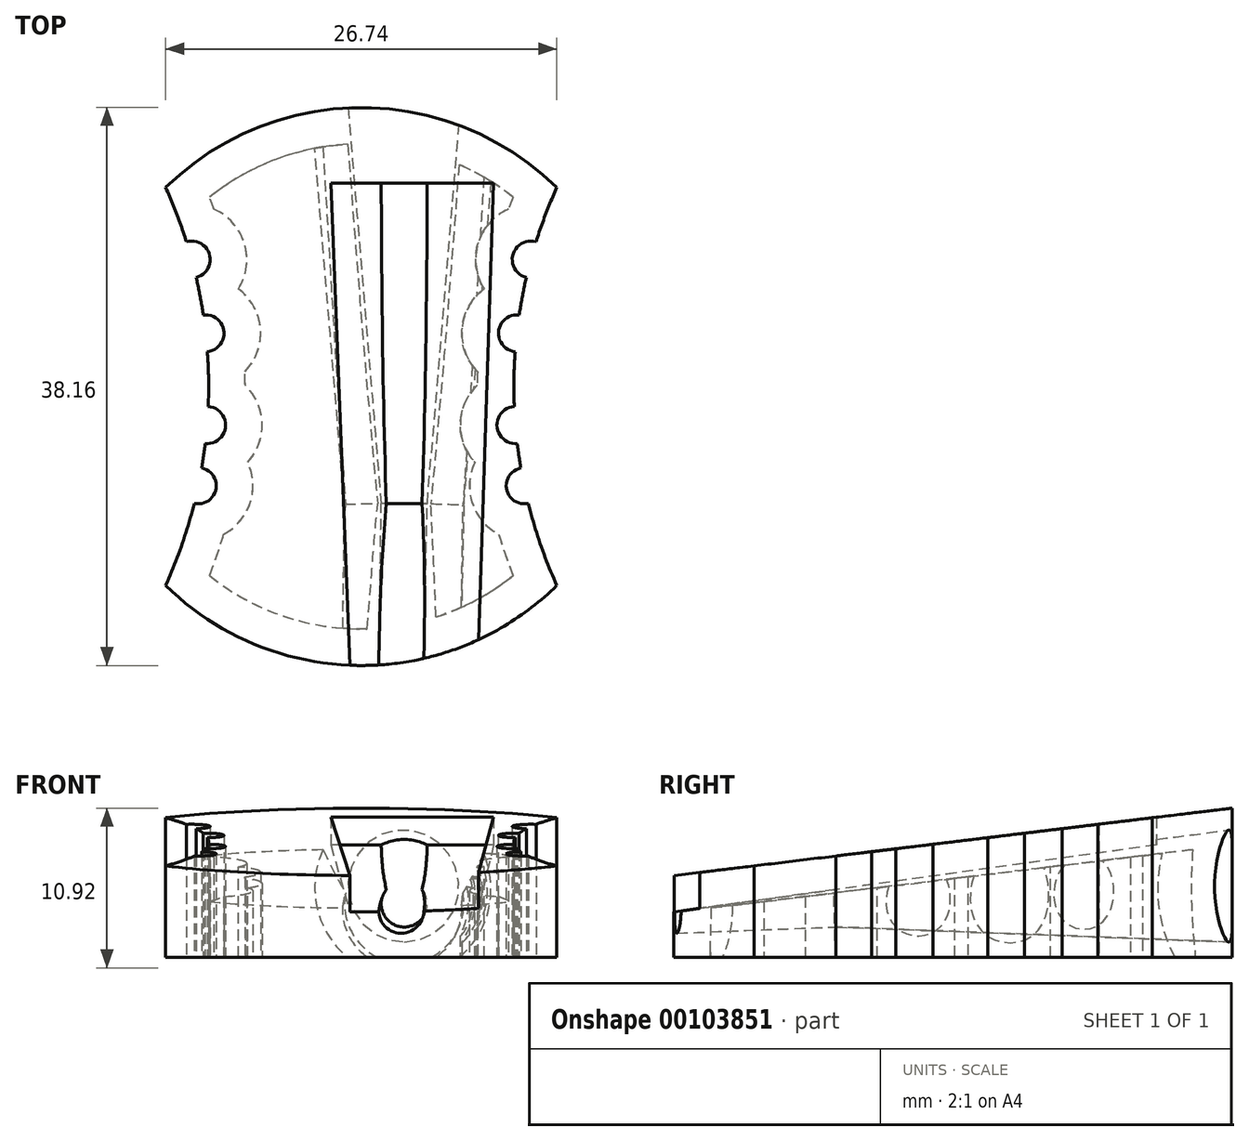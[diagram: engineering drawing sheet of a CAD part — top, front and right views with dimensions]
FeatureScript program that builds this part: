
annotation { "Feature Type Name" : "Feature", "Feature Type Description" : "" }
export const myFeature = defineFeature(function(context is Context, id is Id, definition is map)
    precondition{}
    {
        {
            var Q0;
            Q0=qCreatedBy(makeId("Top.planeOp"),FACE);
            var sketch = newSketch(context, id + "F0", { "sketchPlane" : qUnion([Q0])});
            skArc(sketch, "E0", {"start": v(-13.37, -13.61) * mm, "mid": v(-12.27, -10.85) * mm, "end": v(-11.42, -8) * mm});
            skArc(sketch, "E1", {"start": v(-13.37, -13.61) * mm, "mid": v(-7.22, -17.66) * mm, "end": v(0, -19.08) * mm});
            skLineSegment(sketch, "E2", {"start": v(0, 19.08) * mm, "end": v(0, -19.08) * mm});
            skArc(sketch, "E3.trimOffspring", {"start": v(0, 19.08) * mm, "mid": v(-7.22, 17.66) * mm, "end": v(-13.37, 13.61) * mm});
            skArc(sketch, "E4", {"start": v(-11.28, 7.44) * mm, "mid": v(-10.36, 9) * mm, "end": v(-11.95, 9.9) * mm});
            skArc(sketch, "E5", {"start": v(-10.52, 2.38) * mm, "mid": v(-9.38, 3.78) * mm, "end": v(-10.8, 4.89) * mm});
            skArc(sketch, "E6", {"start": v(-10.66, -3.9) * mm, "mid": v(-9.27, -2.74) * mm, "end": v(-10.46, -1.38) * mm});
            skArc(sketch, "E7", {"start": v(-11.42, -8) * mm, "mid": v(-9.93, -7.05) * mm, "end": v(-10.9, -5.58) * mm});
            skArc(sketch, "E8.trimOffspring", {"start": v(-11.95, 9.9) * mm, "mid": v(-12.6, 11.77) * mm, "end": v(-13.37, 13.61) * mm});
            skArc(sketch, "E9.trimOffspring", {"start": v(-10.8, 4.89) * mm, "mid": v(-11.01, 6.17) * mm, "end": v(-11.28, 7.44) * mm});
            skArc(sketch, "E10.trimOffspring", {"start": v(-10.46, -1.38) * mm, "mid": v(-10.44, 0.5) * mm, "end": v(-10.52, 2.38) * mm});
            skArc(sketch, "E11.trimOffspring", {"start": v(-10.9, -5.58) * mm, "mid": v(-10.77, -4.74) * mm, "end": v(-10.66, -3.9) * mm});
            skSolve(sketch);
        }
        {
            var Q0;
            Q0=makeQuery(id+"F0.imprint","IMPRINT",FACE,{"disambiguationData":[TD([[makeQuery(id+"F0.imprint","IMPRINT",EDGE,{"derivedFrom":sQuery(id+"F0.wireOp",EDGE,"E0")}),-1.0]])]});
            extrude(context, id + "F1", {"entities" : qUnion([Q0]), "depth" : 10.65 * mm});
        }
        {
            var Q0;
            Q0=makeQuery(id+"F1.opExtrude","SWEPT_BODY",BODY,{"disambiguationData":[OSD([sQuery(id+"F0.wireOp",EDGE,"E0"),sQuery(id+"F0.wireOp",EDGE,"E1"),sQuery(id+"F0.wireOp",EDGE,"E2"),sQuery(id+"F0.wireOp",EDGE,"E3.trimOffspring"),sQuery(id+"F0.wireOp",EDGE,"E4"),sQuery(id+"F0.wireOp",EDGE,"E5"),sQuery(id+"F0.wireOp",EDGE,"E6"),sQuery(id+"F0.wireOp",EDGE,"E7"),sQuery(id+"F0.wireOp",EDGE,"E8.trimOffspring"),sQuery(id+"F0.wireOp",EDGE,"E9.trimOffspring"),sQuery(id+"F0.wireOp",EDGE,"E10.trimOffspring"),sQuery(id+"F0.wireOp",EDGE,"E11.trimOffspring")])]});
            var Q1;
            Q1=qCreatedBy(makeId("Right.planeOp"),FACE);
            mirror(context, id + "F2", {"operationType" : NewBodyOperationType.ADD, "entities" : qUnion([Q0]), "mirrorPlane" : qUnion([Q1])});
        }
        {
            var Q0;
            Q0=qCreatedBy(makeId("Right.planeOp"),FACE);
            var sketch = newSketch(context, id + "F3", { "sketchPlane" : qUnion([Q0])});
            skLineSegment(sketch, "E12.bottom", {"start": v(-40.05, 29.12) * mm, "end": v(37.12, 29.12) * mm});
            skLineSegment(sketch, "E12.top", {"start": v(-40.05, 0) * mm, "end": v(37.12, 0) * mm});
            skLineSegment(sketch, "E12.left", {"start": v(-40.05, 29.12) * mm, "end": v(-40.05, 0) * mm});
            skLineSegment(sketch, "E12.right", {"start": v(37.12, 29.12) * mm, "end": v(37.12, 0) * mm});
            skLineSegment(sketch, "E13", {"start": v(-40.05, 3.06) * mm, "end": v(37.12, 12.38) * mm});
            skSolve(sketch);
        }
        {
            var Q0;
            {var subQ0=sQuery(id+"F3.wireOp",EDGE,"E12.bottom");Q0=makeQuery(id+"F3.imprint","IMPRINT",FACE,{"disambiguationData":[TD([[makeQuery(id+"F3.imprint","IMPRINT",EDGE,{"derivedFrom":subQ0}),-1.0]])]});}
            extrude(context, id + "F4", {"entities" : qUnion([Q0]), "operationType" : NewBodyOperationType.REMOVE, "endBound" : BoundingType.SYMMETRIC, "depth" : 39.64 * mm});
        }
        {
            var Q0;
            Q0=qCreatedBy(makeId("Front.planeOp"),FACE);
            cPlane(context, id + "F5", {"entities" : qUnion([Q0]), "cplaneType" : CPlaneType.OFFSET, "offset" : 19.08 * mm, "oppositeDirection" : true, "width" : 150 * mm, "height" : 150 * mm});
        }
        {
            var Q0;
            Q0=qCreatedBy(id+"F5.planeOp",FACE);
            var sketch = newSketch(context, id + "F6", { "sketchPlane" : qUnion([Q0])});
            skLineSegment(sketch, "E14", {"start": v(6.78, 7.67) * mm, "end": v(6.78, 0.5) * mm});
            skLineSegment(sketch, "E15", {"start": v(9.61, 8.73) * mm, "end": v(2.64, 8.73) * mm});
            skCircle(sketch, "E16", {"center": v(2.94, 4.89) * mm, "radius": 3.84 * mm});
            skSolve(sketch);
        }
        {
            var Q0;
            Q0=qCreatedBy(makeId("Front.planeOp"),FACE);
            cPlane(context, id + "F7", {"entities" : qUnion([Q0]), "cplaneType" : CPlaneType.OFFSET, "offset" : 8 * mm, "width" : 150 * mm, "height" : 150 * mm});
        }
        {
            var Q0;
            Q0=qCreatedBy(id+"F7.planeOp",FACE);
            var sketch = newSketch(context, id + "F8", { "sketchPlane" : qUnion([Q0])});
            skCircle(sketch, "E17", {"center": v(2.94, 3.65) * mm, "radius": 1.58 * mm});
            skSolve(sketch);
        }
        {
            var Q1;
            Q1 = qSketchRegion(id + "F8", true);
            var Q2;
            Q2 = qSketchRegion(id + "F6", true);
            loft(context, id + "F9", {"operationType" : NewBodyOperationType.REMOVE, "sheetProfilesArray" : [{ "sheetProfileEntities" : qUnion([Q1]) }, { "sheetProfileEntities" : qUnion([Q2]) }]});
        }
        {
            var Q0;
            Q0=qCreatedBy(makeId("Front.planeOp"),FACE);
            cPlane(context, id + "F10", {"entities" : qUnion([Q0]), "cplaneType" : CPlaneType.OFFSET, "offset" : 19.08 * mm, "width" : 150 * mm, "height" : 150 * mm});
        }
        {
            var Q0;
            Q0=qCreatedBy(id+"F10.planeOp",FACE);
            var sketch = newSketch(context, id + "F11", { "sketchPlane" : qUnion([Q0])});
            skCircle(sketch, "E18", {"center": v(2.74, 3.18) * mm, "radius": 1.54 * mm});
            skSolve(sketch);
        }
        {
            var Q1;
            Q1 = qSketchRegion(id + "F8", true);
            var Q2;
            Q2 = qSketchRegion(id + "F11", true);
            loft(context, id + "F12", {"operationType" : NewBodyOperationType.REMOVE, "sheetProfilesArray" : [{ "sheetProfileEntities" : qUnion([Q1]) }, { "sheetProfileEntities" : qUnion([Q2]) }]});
        }
        {
            var Q0;
            {var subQ0=makeQuery(id+"F1.opExtrude","CAP_FACE",FACE,{"disambiguationData":[OSD([sQuery(id+"F0.wireOp",EDGE,"E0"),sQuery(id+"F0.wireOp",EDGE,"E1"),sQuery(id+"F0.wireOp",EDGE,"E2"),sQuery(id+"F0.wireOp",EDGE,"E3.trimOffspring"),sQuery(id+"F0.wireOp",EDGE,"E4"),sQuery(id+"F0.wireOp",EDGE,"E5"),sQuery(id+"F0.wireOp",EDGE,"E6"),sQuery(id+"F0.wireOp",EDGE,"E7"),sQuery(id+"F0.wireOp",EDGE,"E8.trimOffspring"),sQuery(id+"F0.wireOp",EDGE,"E9.trimOffspring"),sQuery(id+"F0.wireOp",EDGE,"E10.trimOffspring"),sQuery(id+"F0.wireOp",EDGE,"E11.trimOffspring")])],"isStart":true});Q0=makeQuery(id+"F2.boolean.opBoolean","MERGE",FACE,{"derivedFrom":[subQ0,makeQuery(id+"F2.opPattern","COPY",FACE,{"derivedFrom":subQ0,"instanceName":"1"})]});}
            shell(context, id + "F13", {"entities" : qUnion([Q0]), "thickness" : 2.5 * mm});
        }
        {
            var Q0;
            Q0=qCreatedBy(makeId("Front.planeOp"),FACE);
            cPlane(context, id + "F14", {"entities" : qUnion([Q0]), "cplaneType" : CPlaneType.OFFSET, "offset" : 13.9 * mm, "oppositeDirection" : true, "width" : 150 * mm, "height" : 150 * mm});
        }
        {
            var Q0;
            Q0=qCreatedBy(id+"F10.planeOp",FACE);
            var sketch = newSketch(context, id + "F15", { "sketchPlane" : qUnion([Q0])});
            skLineSegment(sketch, "E19.bottom", {"start": v(-0.78, 5.97) * mm, "end": v(7.95, 5.97) * mm});
            skLineSegment(sketch, "E19.top", {"start": v(-0.78, 3.1) * mm, "end": v(7.95, 3.1) * mm});
            skLineSegment(sketch, "E19.left", {"start": v(-0.78, 5.97) * mm, "end": v(-0.78, 3.1) * mm});
            skLineSegment(sketch, "E19.right", {"start": v(7.95, 5.97) * mm, "end": v(7.95, 3.1) * mm});
            skSolve(sketch);
        }
        {
            var Q0;
            Q0=qCreatedBy(id+"F14.planeOp",FACE);
            var sketch = newSketch(context, id + "F16", { "sketchPlane" : qUnion([Q0])});
            skLineSegment(sketch, "E20.bottom", {"start": v(9.04, 10.36) * mm, "end": v(-2.08, 10.36) * mm});
            skLineSegment(sketch, "E20.top", {"start": v(9.04, 7.68) * mm, "end": v(-2.08, 7.68) * mm});
            skLineSegment(sketch, "E20.left", {"start": v(9.04, 10.36) * mm, "end": v(9.04, 7.68) * mm});
            skLineSegment(sketch, "E20.right", {"start": v(-2.08, 10.36) * mm, "end": v(-2.08, 7.68) * mm});
            skSolve(sketch);
        }
        {
            var Q1;
            Q1 = qSketchRegion(id + "F16", true);
            var Q2;
            Q2 = qSketchRegion(id + "F15", true);
            loft(context, id + "F17", {"operationType" : NewBodyOperationType.REMOVE, "sheetProfilesArray" : [{ "sheetProfileEntities" : qUnion([Q1]) }, { "sheetProfileEntities" : qUnion([Q2]) }]});
        }
    });
